FCSTD DOCUMENT  (FreeCAD 0.18R16093 (Git))
Label: motormount_v1
License: All rights reserved
LicenseURL: http://en.wikipedia.org/wiki/All_rights_reserved
objects: Image::ImagePlane×2, Sketcher::SketchObject×2, App::MeasureDistance×1, PartDesign::Body×1
note: 3 computed .brp shape members not serialized (recipe doc carries the construction recipe); baked Part::Feature solids carry a one-line shape summary decoded from their .brp

FEATURE [Image::ImagePlane] ImagePlane  label="topimage"
  Placement = pos=(-5,-14,-1) rot=(0,0,1;0rad)
  XSize = 1028.38
  YSize = 484.38
  expr: YSize = 260 * 1.863
  expr: XSize = 552 * 1.863
FEATURE [Image::ImagePlane] ImagePlane001  label="bottomimage"
  Placement = pos=(0,0,2) rot=(0,1,0;3.14159rad)
  XSize = 981.024
  YSize = 471.932
  expr: YSize = 254 * 1.858
  expr: XSize = 528 * 1.858
FEATURE [App::MeasureDistance] Distance  label="Distance: 497,84 mm"
  Distance = 497.844
  P1 = (247.115,-24.15,-1)
  P2 = (-250.729,-24.3921,-1)
FEATURE [Sketcher::SketchObject] Sketch
  MapMode = 5
  Support = -> [XY_Plane]
  sketch-geometry (16):
    g0: LineSegment StartX=-0.00153 StartY=205.66 StartZ=0 EndX=461.684 EndY=-23.2229 EndZ=0
    g1: LineSegment StartX=461.684 StartY=-23.2229 StartZ=0 EndX=461.684 EndY=-145.856 EndZ=0
    g2: LineSegment StartX=461.684 StartY=-145.856 StartZ=0 EndX=135.863 EndY=-36.5775 EndZ=0
    g3: LineSegment StartX=135.863 StartY=-36.5775 StartZ=0 EndX=110.985 EndY=1.8606 EndZ=0
    g4: LineSegment StartX=110.985 StartY=1.8606 StartZ=0 EndX=19.3718 EndY=1.8606 EndZ=0
    g5: LineSegment StartX=19.3718 StartY=1.8606 StartZ=0 EndX=19.3718 EndY=9.3143 EndZ=0
    g6: LineSegment StartX=19.3718 StartY=9.3143 StartZ=0 EndX=-11.5161 EndY=9.3143 EndZ=0
    g7: LineSegment StartX=-11.5161 StartY=9.3143 StartZ=0 EndX=-11.5161 EndY=0 EndZ=0
    g8: LineSegment StartX=-11.5161 StartY=0 StartZ=0 EndX=-115.045 EndY=0 EndZ=0
    g9: LineSegment StartX=-115.045 StartY=0 StartZ=0 EndX=-132.088 EndY=-32.4305 EndZ=0
    g10: LineSegment StartX=-132.088 StartY=-32.4305 StartZ=0 EndX=-459.667 EndY=-146.353 EndZ=0
    g11: LineSegment StartX=-459.667 StartY=-146.353 StartZ=0 EndX=-459.667 EndY=-28.9063 EndZ=0
    g12: LineSegment StartX=-459.667 StartY=-28.9063 StartZ=0 EndX=-0.00153 EndY=205.66 EndZ=0
    g13: LineSegment StartX=0 StartY=0 StartZ=0 EndX=0 EndY=231.644 EndZ=0
    g14: LineSegment StartX=451.737 StartY=-140.336 StartZ=0 EndX=-461.411 EndY=-140.336 EndZ=0
    g15: LineSegment StartX=0 StartY=0 StartZ=0 EndX=0 EndY=-230.012 EndZ=0
  constraints (26):
    c: Coincident(g0,g1)
    c: Vertical(g1)
    c: Coincident(g1,g2)
    c: Coincident(g3,g4)
    c: Horizontal(g4)
    c: Coincident(g4,g5)
    c: Vertical(g5)
    c: Coincident(g5,g6)
    c: Horizontal(g6)
    c: Coincident(g6,g7)
    c: PointOnObject(g7,g-1)
    c: Vertical(g7)
    c: Coincident(g7,g8)
    c: Horizontal(g8)
    c: Coincident(g8,g9)
    c: Coincident(g10,g11)
    c: Vertical(g11)
    c: Coincident(g11,g12)
    c: Coincident(g12,g0)
    c: Coincident(g13,g-1)
    c: Vertical(g13)
    c: Horizontal(g14)
    c: PointOnObject(g15,g-1)
    c: Vertical(g15)
    c: Coincident(g9,g10)
    c: Coincident(g3,g2)
FEATURE [Sketcher::SketchObject] Sketch001
  MapMode = 5
  Support = -> [XY_Plane]
  expr: Constraints[10] = 28.4 / 2
  sketch-geometry (12):
    g0: LineSegment [constr] StartX=14.2 StartY=5 StartZ=0 EndX=-14.2 EndY=5 EndZ=0
    g1: LineSegment StartX=-14.2 StartY=5 StartZ=0 EndX=-14.2 EndY=0 EndZ=0
    g2: LineSegment StartX=-14.2 StartY=0 StartZ=0 EndX=14.2 EndY=0 EndZ=0
    g3: LineSegment StartX=14.2 StartY=0 StartZ=0 EndX=14.2 EndY=5 EndZ=0
    g4: ArcOfCircle CenterX=-46.7782 CenterY=66.8062 CenterZ=0 NormalX=0 NormalY=0 NormalZ=1 AngleXU=0 Radius=9 StartAngle=0.740667 EndAngle=3.7167
    g5: ArcOfCircle CenterX=46.7782 CenterY=66.8062 CenterZ=0 NormalX=0 NormalY=0 NormalZ=1 AngleXU=0 Radius=9 StartAngle=5.70808 EndAngle=8.68411
    g6: LineSegment StartX=54.3304 StartY=61.9108 StartZ=0 EndX=14.2 EndY=0 EndZ=0
    g7: LineSegment StartX=-14.2 StartY=0 StartZ=0 EndX=-54.3304 EndY=61.9108 EndZ=0
    g8: ArcOfCircle CenterX=0 CenterY=34.9096 CenterZ=0 NormalX=0 NormalY=0 NormalZ=1 AngleXU=0 Radius=4 StartAngle=3.88226 EndAngle=5.54252
    g9: LineSegment StartX=40.136 StartY=72.8792 StartZ=0 EndX=2.95207 EndY=32.2105 EndZ=0
    g10: LineSegment StartX=-40.136 StartY=72.8792 StartZ=0 EndX=-2.95207 EndY=32.2105 EndZ=0
    g11: LineSegment [constr] StartX=0 StartY=0 StartZ=0 EndX=-46.7782 EndY=66.8062 EndZ=0
  constraints (27):
    c: Coincident(g0,g1)
    c: Coincident(g1,g2)
    c: Coincident(g2,g3)
    c: Coincident(g3,g0)
    c: Horizontal(g2)
    c: Vertical(g1)
    c: Vertical(g3)
    c: PointOnObject(g1,g-1)
    c: DistanceY(g1,g1) = 5
    c: Symmetric(g0,g0,g-2)
    c: DistanceX(g1,g-1) = 14.2
    c: Symmetric(g5,g4,g-2)
    c: Equal(g4,g5)
    c: Coincident(g6,g2)
    c: Tangent(g6,g5) = 1.5708
    c: Coincident(g7,g1)
    c: Tangent(g7,g4) = 1.5708
    c: PointOnObject(g8,g-2)
    c: Tangent(g9,g8) = 1.5708
    c: Tangent(g8,g10) = -1.5708
    c: Tangent(g4,g10) = 1.5708
    c: Tangent(g9,g5) = -1.5708
    c: Radius(g5) = 9
    c: Radius(g8) = 4
    c: Coincident(g11,g4)
    c: Coincident(g-1,g11)
    c: Angle(g-1,g11) = 2.18166
FEATURE [PartDesign::Body] Body
  Group = -> [Sketch,Sketch001]
  Origin = -> Origin
